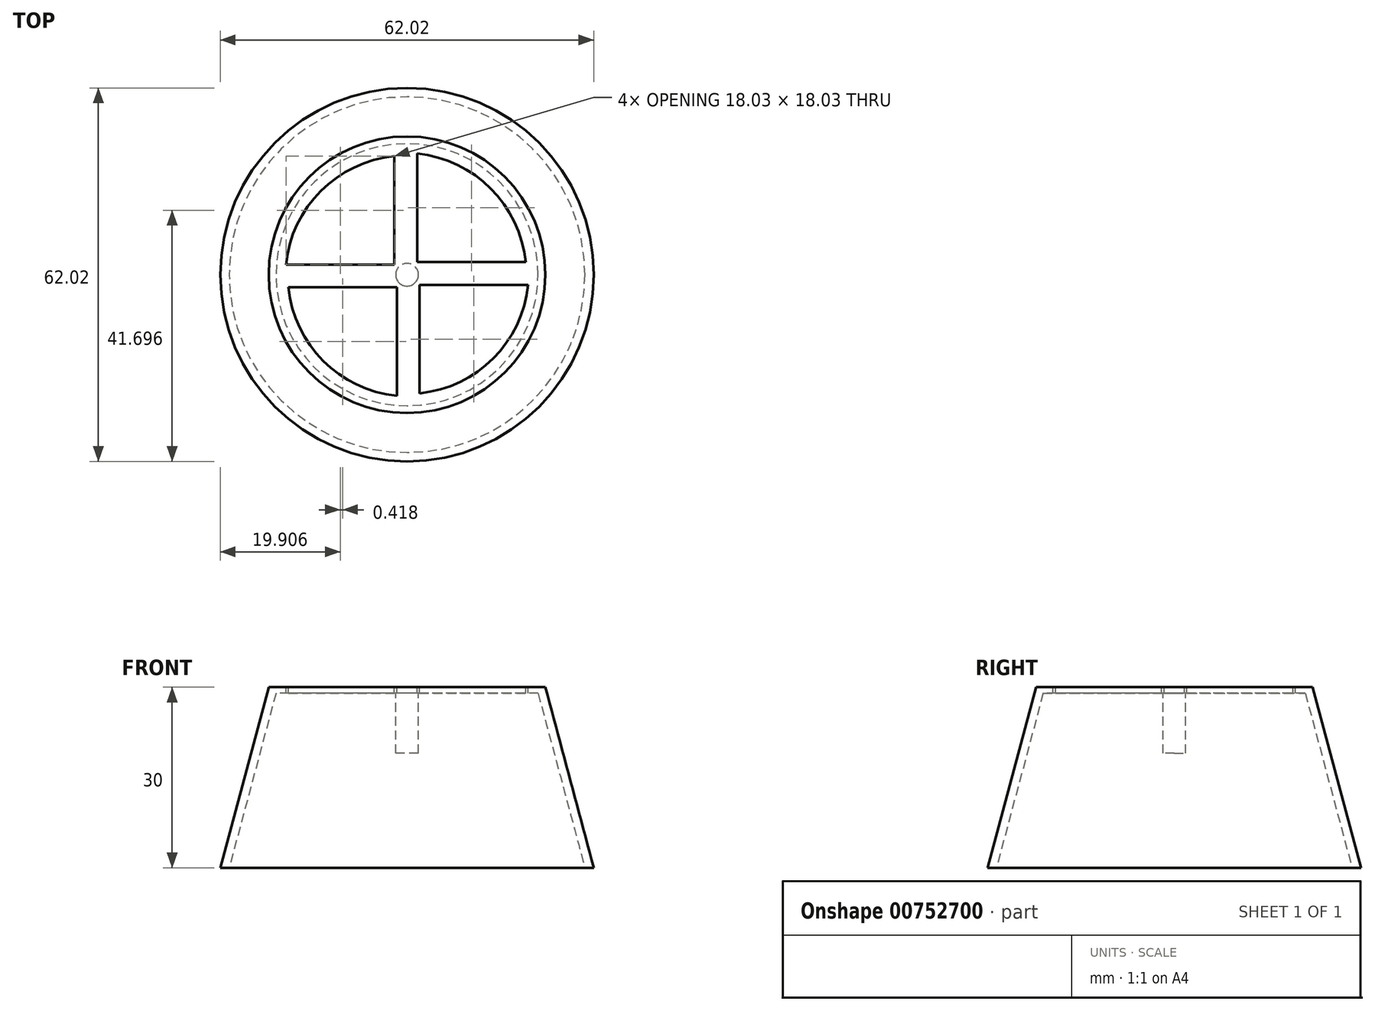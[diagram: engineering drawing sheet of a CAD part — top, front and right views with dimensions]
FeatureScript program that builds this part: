
annotation { "Feature Type Name" : "Feature", "Feature Type Description" : "" }
export const myFeature = defineFeature(function(context is Context, id is Id, definition is map)
    precondition{}
    {
        {
            var Q0;
            Q0=qCreatedBy(makeId("Front.planeOp"),FACE);
            var sketch = newSketch(context, id + "F0", { "sketchPlane" : qUnion([Q0])});
            skLineSegment(sketch, "E0", {"start": v(0, 0) * mm, "end": v(31, 0) * mm});
            skLineSegment(sketch, "E1", {"start": v(31, 0) * mm, "end": v(22.97, 30) * mm});
            skLineSegment(sketch, "E2", {"start": v(22.97, 30) * mm, "end": v(0, 30) * mm});
            skLineSegment(sketch, "E3", {"start": v(0, 30) * mm, "end": v(0, 0) * mm});
            skLineSegment(sketch, "E4", {"start": v(0, 29) * mm, "end": v(21.77, 29) * mm});
            skLineSegment(sketch, "E5", {"start": v(21.77, 29) * mm, "end": v(29.54, 0) * mm});
            skSolve(sketch);
        }
        {
            var Q0;
            {var subQ3=sQuery(id+"F0.wireOp",EDGE,"E1");Q0=makeQuery(id+"F0.imprint","IMPRINT",FACE,{"disambiguationData":[TD([[makeQuery(id+"F0.imprint","IMPRINT",EDGE,{"derivedFrom":subQ3}),1.0]])]});}
            var Q1;
            Q1=sQuery(id+"F0.wireOp",EDGE,"E3");
            revolve(context, id + "F1", {"surfaceOperationType" : NewSurfaceOperationType.NEW, "entities" : qUnion([Q0]), "axis" : qUnion([Q1]), "revolveType" : RevolveType.FULL});
        }
        {
            var Q0;
            Q0=makeQuery(id+"F1.opRevolve","SWEPT_FACE",FACE,{"disambiguationData":[OSD([sQuery(id+"F0.wireOp",EDGE,"E2")])]});
            var sketch = newSketch(context, id + "F2", { "sketchPlane" : qUnion([Q0])});
            skLineSegment(sketch, "E6", {"start": v(1.67, 2.09) * mm, "end": v(1.67, 20.12) * mm});
            skLineSegment(sketch, "E7", {"start": v(19.7, 2.09) * mm, "end": v(1.67, 2.09) * mm});
            skArc(sketch, "E8", {"start": v(19.7, 2.09) * mm, "mid": v(13.9, 14.32) * mm, "end": v(1.67, 20.12) * mm});
            skArc(sketch, "E9.1.0", {"start": v(-2.09, 19.7) * mm, "mid": v(-14.32, 13.9) * mm, "end": v(-20.12, 1.67) * mm});
            skLineSegment(sketch, "E9.1.1", {"start": v(-2.09, 1.67) * mm, "end": v(-20.12, 1.67) * mm});
            skLineSegment(sketch, "E9.1.2", {"start": v(-2.09, 19.7) * mm, "end": v(-2.09, 1.67) * mm});
            skArc(sketch, "E9.2.0", {"start": v(-19.7, -2.09) * mm, "mid": v(-13.9, -14.32) * mm, "end": v(-1.67, -20.12) * mm});
            skLineSegment(sketch, "E9.2.1", {"start": v(-1.67, -2.09) * mm, "end": v(-1.67, -20.12) * mm});
            skLineSegment(sketch, "E9.2.2", {"start": v(-19.7, -2.09) * mm, "end": v(-1.67, -2.09) * mm});
            skArc(sketch, "E9.3.0", {"start": v(2.09, -19.7) * mm, "mid": v(14.32, -13.9) * mm, "end": v(20.12, -1.67) * mm});
            skLineSegment(sketch, "E9.3.1", {"start": v(2.09, -1.67) * mm, "end": v(20.12, -1.67) * mm});
            skLineSegment(sketch, "E9.3.2", {"start": v(2.09, -19.7) * mm, "end": v(2.09, -1.67) * mm});
            skPoint(sketch, "E9.center", {"position": v(0, 0) * mm});
            skSolve(sketch);
        }
        {
            var Q0;
            Q0=makeQuery(id+"F2.imprint","IMPRINT",FACE,{"disambiguationData":[TD([[makeQuery(id+"F2.imprint","IMPRINT",EDGE,{"derivedFrom":sQuery(id+"F2.wireOp",EDGE,"E9.1.0")}),1.0]])]});
            var Q1;
            Q1=makeQuery(id+"F2.imprint","IMPRINT",FACE,{"disambiguationData":[TD([[makeQuery(id+"F2.imprint","IMPRINT",EDGE,{"derivedFrom":sQuery(id+"F2.wireOp",EDGE,"E6")}),-1.0]])]});
            var Q2;
            Q2=makeQuery(id+"F2.imprint","IMPRINT",FACE,{"disambiguationData":[TD([[makeQuery(id+"F2.imprint","IMPRINT",EDGE,{"derivedFrom":sQuery(id+"F2.wireOp",EDGE,"E9.2.0")}),1.0]])]});
            var Q3;
            Q3=makeQuery(id+"F2.imprint","IMPRINT",FACE,{"disambiguationData":[TD([[makeQuery(id+"F2.imprint","IMPRINT",EDGE,{"derivedFrom":sQuery(id+"F2.wireOp",EDGE,"E9.3.0")}),1.0]])]});
            extrude(context, id + "F3", {"entities" : qUnion([Q0, Q1, Q2, Q3]), "operationType" : NewBodyOperationType.REMOVE, "oppositeDirection" : true, "depth" : 25 * mm, "offsetDistance" : 25 * mm});
        }
        {
            var Q0;
            Q0=makeQuery(id+"F1.opRevolve","SWEPT_FACE",FACE,{"disambiguationData":[OSD([sQuery(id+"F0.wireOp",EDGE,"E4")])]});
            var sketch = newSketch(context, id + "F4", { "sketchPlane" : qUnion([Q0])});
            skCircle(sketch, "E10", {"center": v(0, 0) * mm, "radius": 1.89 * mm});
            skSolve(sketch);
        }
        {
            var Q0;
            Q0=makeQuery(id+"F4.imprint","IMPRINT",FACE,{"disambiguationData":[TD([[makeQuery(id+"F4.imprint","IMPRINT",EDGE,{"derivedFrom":sQuery(id+"F4.wireOp",EDGE,"E10")}),1.0]])]});
            extrude(context, id + "F5", {"entities" : qUnion([Q0]), "operationType" : NewBodyOperationType.ADD, "depth" : 10 * mm, "offsetDistance" : 25 * mm});
        }
    });
